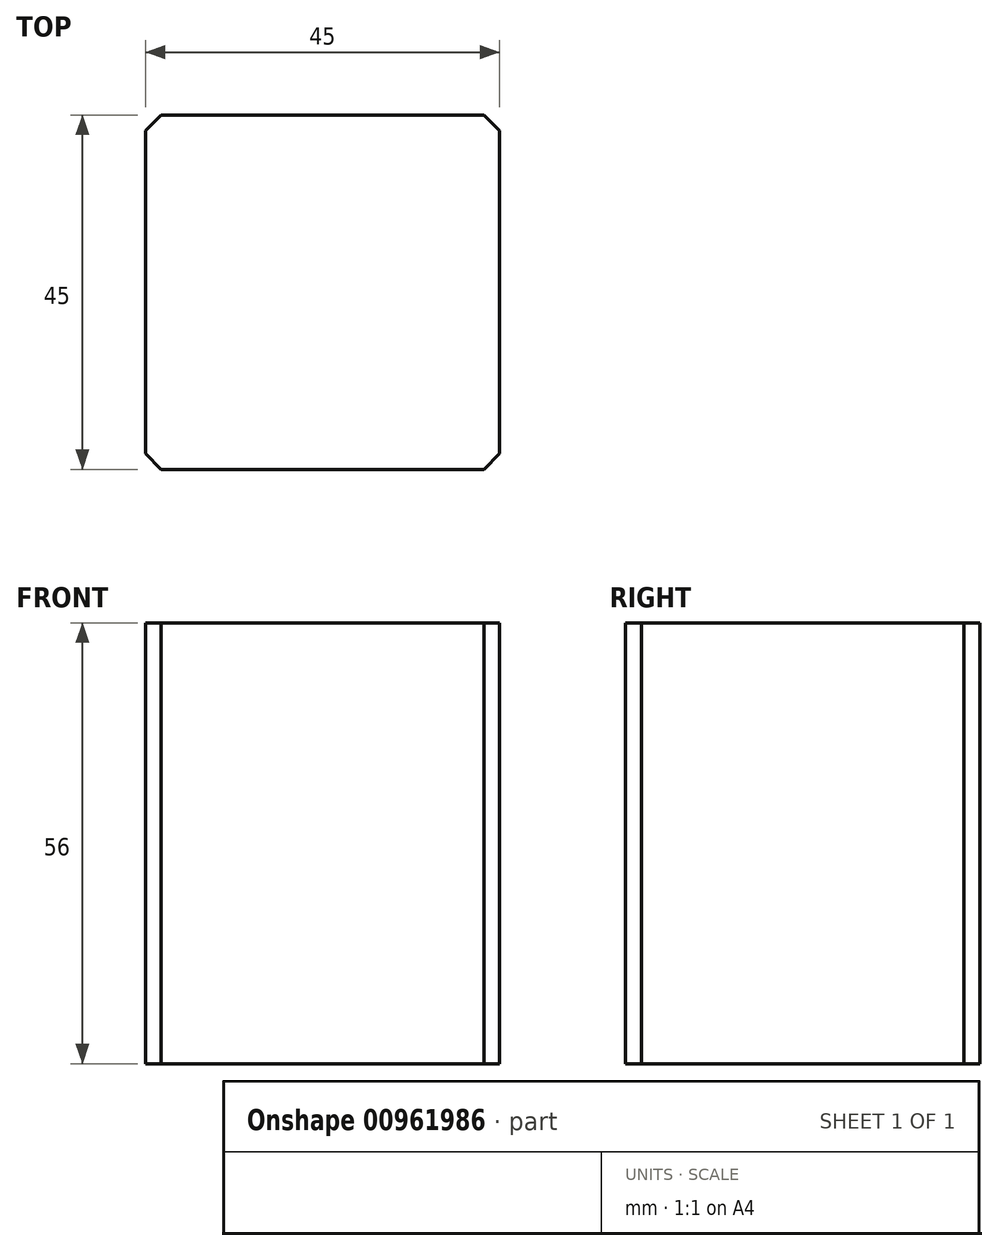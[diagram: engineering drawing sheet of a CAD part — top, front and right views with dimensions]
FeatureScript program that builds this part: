
annotation { "Feature Type Name" : "Feature", "Feature Type Description" : "" }
export const myFeature = defineFeature(function(context is Context, id is Id, definition is map)
    precondition{}
    {
        {
            var Q0;
            Q0=qCreatedBy(makeId("Top.planeOp"),FACE);
            var sketch = newSketch(context, id + "F0", { "sketchPlane" : qUnion([Q0])});
            skLineSegment(sketch, "E0.bottom", {"start": v(22.5, 22.5) * mm, "end": v(-22.5, 22.5) * mm});
            skLineSegment(sketch, "E0.top", {"start": v(22.5, -22.5) * mm, "end": v(-22.5, -22.5) * mm});
            skLineSegment(sketch, "E0.left", {"start": v(22.5, 22.5) * mm, "end": v(22.5, -22.5) * mm});
            skLineSegment(sketch, "E0.right", {"start": v(-22.5, 22.5) * mm, "end": v(-22.5, -22.5) * mm});
            skPoint(sketch, "E0.middle", {"position": v(0, 0) * mm});
            skSolve(sketch);
        }
        {
            var Q0;
            Q0=makeQuery(id+"F0.imprint","IMPRINT",FACE,{"disambiguationData":[TD([[makeQuery(id+"F0.imprint","IMPRINT",EDGE,{"derivedFrom":sQuery(id+"F0.wireOp",EDGE,"E0.bottom")}),1.0]])]});
            extrude(context, id + "F1", {"entities" : qUnion([Q0]), "oppositeDirection" : true, "depth" : 52 * mm, "offsetDistance" : 25 * mm, "hasSecondDirection" : true, "secondDirectionOppositeDirection" : false, "secondDirectionDepth" : 4 * mm});
        }
        {
            var Q0;
            Q0=makeQuery(id+"F1.opExtrude","SWEPT_EDGE",EDGE,{"disambiguationData":[OSD([sQuery(id+"F0.wireOp",EDGE,"E0.bottom"),sQuery(id+"F0.wireOp",EDGE,"E0.right")])]});
            var Q1;
            Q1=makeQuery(id+"F1.opExtrude","SWEPT_EDGE",EDGE,{"disambiguationData":[OSD([sQuery(id+"F0.wireOp",EDGE,"E0.bottom"),sQuery(id+"F0.wireOp",EDGE,"E0.left")])]});
            var Q2;
            Q2=makeQuery(id+"F1.opExtrude","SWEPT_EDGE",EDGE,{"disambiguationData":[OSD([sQuery(id+"F0.wireOp",EDGE,"E0.top"),sQuery(id+"F0.wireOp",EDGE,"E0.left")])]});
            var Q3;
            Q3=makeQuery(id+"F1.opExtrude","SWEPT_EDGE",EDGE,{"disambiguationData":[OSD([sQuery(id+"F0.wireOp",EDGE,"E0.top"),sQuery(id+"F0.wireOp",EDGE,"E0.right")])]});
            chamfer(context, id + "F2", {"entities" : qUnion([Q0, Q1, Q2, Q3]), "width" : 2 * mm, "tangentPropagation" : true});
        }
    });
